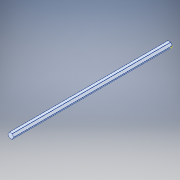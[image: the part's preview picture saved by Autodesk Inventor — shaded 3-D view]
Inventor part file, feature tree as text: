
AUTODESK INVENTOR PART (.ipt)
format: ipt  version: 2017 (Build 210142000, 142)  size: 158,208 bytes
history: native  units: in
note: dims shown in document units (in); Inventor stores cm internally (conversion verified against a paired STEP export)
features: sketch x6, split x1, fillet x1
ambient origin geometry x8: Origin, YZ Plane, XZ Plane, XY Plane, X Axis, Y Axis, Z Axis, Center Point
bodies: Solid1 (feature_tree)
feature tree (8):
  sketch  "Sketch1"  dims[d11=16.0in]
  split  "Split1"
  sketch  "Sketch3"  dims[d13=7.8125in]
  sketch  "Sketch4"  dims[d14=3.5453in]
  sketch  "Sketch5"  dims[d15=3.5453in]
  sketch  "Sketch7"
  sketch  "Sketch2"  dims[d12=7.8125in]
  fillet  "Fillet1"  Radius=8.5in
